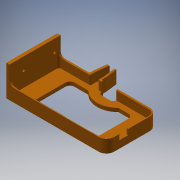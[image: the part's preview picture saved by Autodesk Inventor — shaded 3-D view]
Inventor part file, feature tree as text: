
AUTODESK INVENTOR PART (.ipt)
format: ipt  version: 2017 (Build 210142000, 142)  size: 463,872 bytes
history: native  units: in
note: dims shown in document units (in); Inventor stores cm internally (conversion verified against a paired STEP export)
features: sketch x20, extrude x19, fillet x11, thicken_offset x4, projected_geometry x4, hole x1
ambient origin geometry x8: Origin, YZ Plane, XZ Plane, XY Plane, X Axis, Y Axis, Z Axis, Center Point
bodies: Solid1 (feature_tree)
feature tree (59):
  extrude  "Extrusion1"  Depth=2.655in
  extrude  "Extrusion2"  Depth=0.5in TaperAngle=0.0deg
  fillet  "Fillet1"  Radius=0.2in
  fillet  "Fillet2"  Radius=0.3in
  extrude  "Extrusion3"  Depth=0.42in
  extrude  "Extrusion4"  Depth=0.125in
  extrude  "Extrusion5"  Depth=0.125in
  fillet  "Fillet3"  Radius=0.125in
  fillet  "Fillet4"  Radius=0.125in
  fillet  "Fillet5"  Radius=0.125in
  extrude  "Extrusion6"  Depth=0.125in TaperAngle=0.0deg
  fillet  "Fillet6"  Radius=0.06in
  extrude  "Extrusion8"  Depth=0.25in
  fillet  "Fillet7"  Radius=0.25in
  extrude  "Extrusion10"  TaperAngle=0.0deg  [1 undecoded]
  extrude  "Extrusion11"  Depth=1.0in TaperAngle=0.0deg
  extrude  "Extrusion13"  Depth=1.1887in
  thicken_offset  "Thicken1"
  extrude  "Extrusion14"  Depth=1.932in
  sketch  "Sketch15"  dims[d57=0.25in d58=1.0in d59=0.0in]
  fillet  "Fillet10"  Radius=0.9in
  extrude  "Extrusion17"  Depth=0.3in
  fillet  "Fillet11"  Radius=0.3in
  thicken_offset  "Thicken2"
  thicken_offset  "Thicken3"
  thicken_offset  "Thicken4"
  extrude  "Extrusion18"  Depth=0.25in TaperAngle=0.0deg
  extrude  "Extrusion19"  Depth=0.48in
  extrude  "Extrusion20"  Depth=0.3in TaperAngle=0.0deg
  extrude  "Extrusion21"  TaperAngle=0.0deg  [1 undecoded]
  extrude  "Extrusion22"  Depth=0.875in
  extrude  "Extrusion23"  Depth=0.04in
  fillet  "Fillet12"  Radius=1.0in
  fillet  "Fillet13"  Radius=0.5in
  hole  "Hole1"  [1 undecoded]
  extrude  "Extrusion12"  Depth=0.25in
  sketch  "Sketch1"  dims[d0=5.265in d1=2.655in]
  sketch  "Sketch2"  dims[d2=0.08in d3=0.5in d4=0.0in d5=0.2in d6=0.0in d7=0.3in]
  sketch  "Sketch3"  dims[d8=0.425in d9=0.42in]
  sketch  "Sketch4"  dims[d10=0.125in d11=0.0in d14=0.2275in]
  sketch  "Sketch5"  dims[d15=0.9in d17=0.125in d18=0.125in d19=0.125in d20=0.125in]
  sketch  "Sketch6"  dims[d21=0.0in d22=0.0in d23=0.125in d24=0.0in d25=0.06in]
  sketch  "Sketch8"  dims[d26=0.06in d27=0.04in d29=0.25in]
  sketch  "Sketch10"  dims[d30=2.75in d31=0.0in d32=0.0in]
  sketch  "Sketch11"  dims[d33=0.16in d43=1.0in d44=0.0in]
  sketch  "Sketch12"  dims[d45=1.1887in d46=1.1887in]
  sketch  "Sketch13"  dims[d47=0.2549in d50=1.932in d53=0.9in]
  sketch  "Sketch14"  dims[d54=0.9in d55=0.3in d56=0.3in]
  projected_geometry  "Projected Loop1"
  projected_geometry  "Projected Loop2"
  projected_geometry  "Projected Loop3"
  sketch  "Sketch17"  dims[d61=0.8in d62=0.48in]
  sketch  "Sketch18"  dims[d63=0.88in d64=0.3in d65=0.0in]
  sketch  "Sketch19"  dims[d66=2.0in d67=0.0in d72=0.0in]
  sketch  "Sketch20"  dims[d73=0.0in d74=0.875in]
  sketch  "Sketch21"  dims[d75=1.0in d77=0.04in d78=1.0in d79=0.0in d80=0.5in]
  sketch  "Sketch22"  dims[d81=0.5in d82=0.1in d83=0.0in]
  sketch  "Sketch23"  dims[d88=0.18in d89=0.14in d92=0.1in d93=0.625in d94=1.25in d95=0.0in d96=0.0in d97=0.125in d98=0.375in d99=0.375in d100=0.55in d101=0.55in d102=0.125in d103=0.125in d104=1.0in d105=0.0in d106=1.0in d107=0.0in d108=1.0in d109=0.0in d110=1.0in d111=0.0in d112=1.0in d113=0.0in d114=1.0in d115=0.0in d116=0.25in d117=0.125in d118=0.678in d119=0.678in d120=0.32in d121=2.026in d122=0.14in d123=0.75in d124=0.375in d125=0.25in d126=0.5635in d127=1.0in d128=0.8108in]
  projected_geometry  "Projected Loop4"
note: 3 required parameter values undecoded (feature->parameter linkage not recoverable at this tier; creation-order binding heuristic only, values carry confidence <= 0.55)
